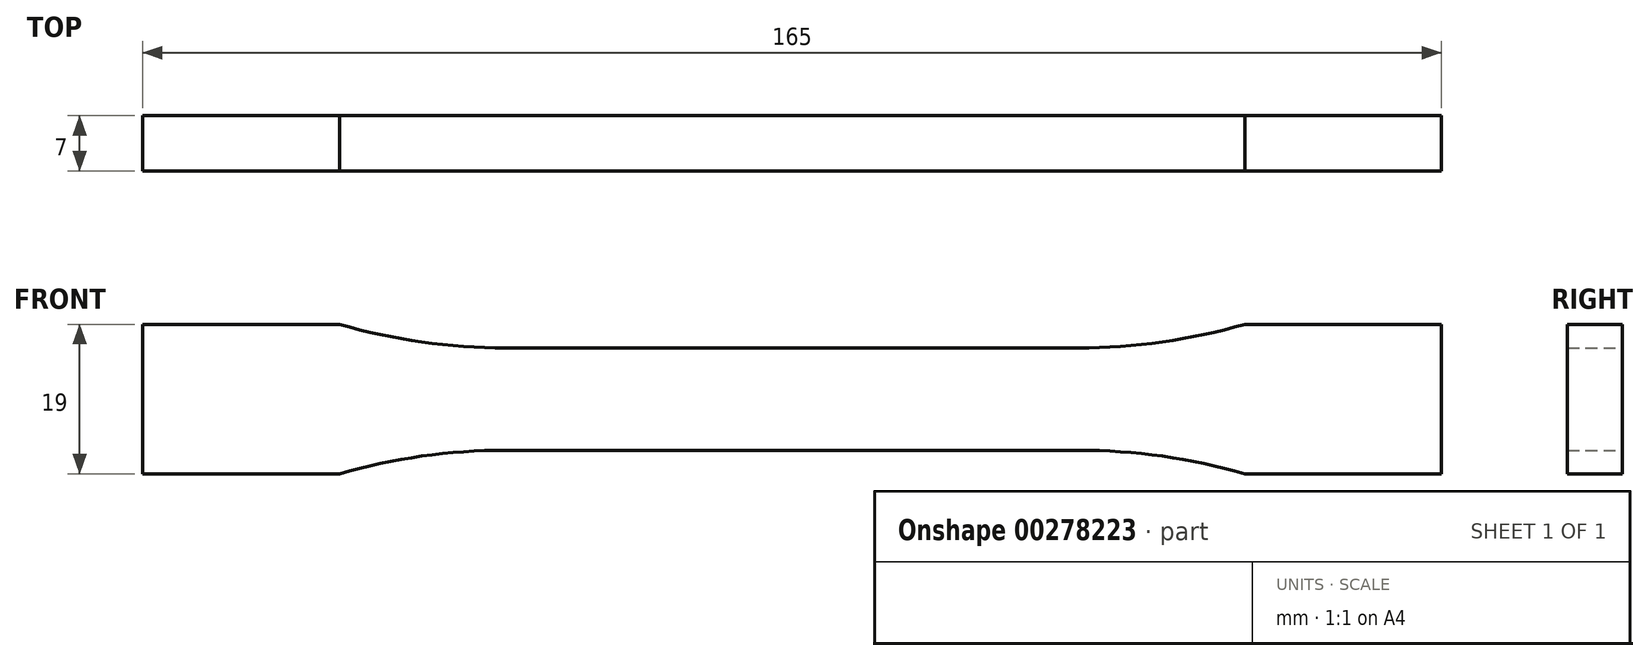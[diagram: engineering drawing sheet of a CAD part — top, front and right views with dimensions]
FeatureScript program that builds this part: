
annotation { "Feature Type Name" : "Feature", "Feature Type Description" : "" }
export const myFeature = defineFeature(function(context is Context, id is Id, definition is map)
    precondition{}
    {
        {
            var Q0;
            Q0=qCreatedBy(makeId("Front.planeOp"),FACE);
            var sketch = newSketch(context, id + "F0", { "sketchPlane" : qUnion([Q0])});
            skLineSegment(sketch, "E0", {"start": v(0, 6.5) * mm, "end": v(36.36, 6.5) * mm});
            skArc(sketch, "E1", {"start": v(36.36, 6.5) * mm, "mid": v(47.03, 7.25) * mm, "end": v(57.5, 9.5) * mm});
            skLineSegment(sketch, "E2", {"start": v(57.5, 9.5) * mm, "end": v(82.5, 9.5) * mm});
            skLineSegment(sketch, "E3.MirrorCS", {"start": v(0, -6.5) * mm, "end": v(36.36, -6.5) * mm});
            skLineSegment(sketch, "E4.MirrorCS", {"start": v(57.5, -9.5) * mm, "end": v(82.5, -9.5) * mm});
            skArc(sketch, "E5.MirrorCS", {"start": v(36.36, -6.5) * mm, "mid": v(47.03, -7.25) * mm, "end": v(57.5, -9.5) * mm});
            skLineSegment(sketch, "E6.MirrorCS", {"start": v(-57.5, 9.5) * mm, "end": v(-82.5, 9.5) * mm});
            skLineSegment(sketch, "E7.MirrorCS", {"start": v(0, -6.5) * mm, "end": v(-36.36, -6.5) * mm});
            skLineSegment(sketch, "E8.MirrorCS", {"start": v(0, 6.5) * mm, "end": v(-36.36, 6.5) * mm});
            skLineSegment(sketch, "E9.MirrorCS", {"start": v(-57.5, -9.5) * mm, "end": v(-82.5, -9.5) * mm});
            skArc(sketch, "E10.MirrorCS", {"start": v(-36.36, 6.5) * mm, "mid": v(-47.03, 7.25) * mm, "end": v(-57.5, 9.5) * mm});
            skArc(sketch, "E11.MirrorCS", {"start": v(-36.36, -6.5) * mm, "mid": v(-47.03, -7.25) * mm, "end": v(-57.5, -9.5) * mm});
            skLineSegment(sketch, "E12", {"start": v(-82.5, 9.5) * mm, "end": v(-82.5, -9.5) * mm});
            skLineSegment(sketch, "E13", {"start": v(82.5, 9.5) * mm, "end": v(82.5, -9.5) * mm});
            skSolve(sketch);
        }
        {
            var Q0;
            Q0 = qSketchRegion(id + "F0", true);
            extrude(context, id + "F1", {"entities" : qUnion([Q0]), "endBound" : BoundingType.SYMMETRIC, "depth" : 7 * mm});
        }
    });
